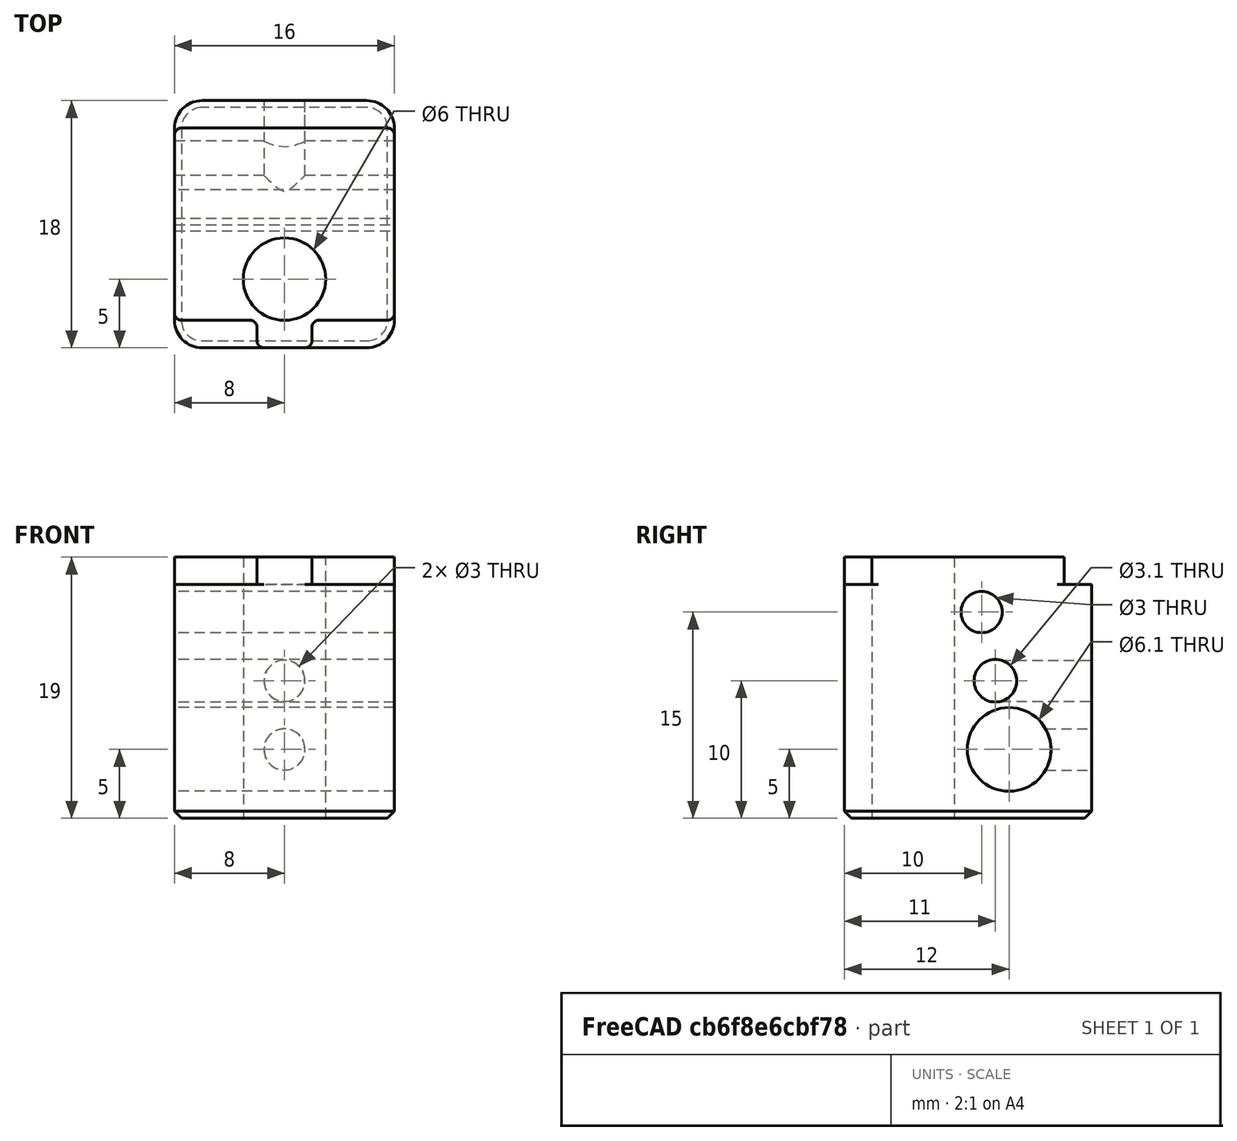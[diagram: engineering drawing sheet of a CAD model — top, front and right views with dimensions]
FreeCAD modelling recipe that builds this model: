
FCSTD DOCUMENT  (FreeCAD 0.17R11850 (Git))
Label: some_struder_heater_block
License: All rights reserved
LicenseURL: http://en.wikipedia.org/wiki/All_rights_reserved
objects: Drawing::FeatureView×33, Sketcher::SketchObject×4, Drawing::FeatureViewPart×4, PartDesign::Pocket×3, PartDesign::Fillet×2, PartDesign::Pad×1, PartDesign::Chamfer×1, PartDesign::Body×1, Drawing::FeaturePage×1
note: 16 computed .brp shape members not serialized (recipe doc carries the construction recipe); baked Part::Feature solids carry a one-line shape summary decoded from their .brp

FEATURE [Sketcher::SketchObject] Sketch
  MapMode = 5
  Support = -> [XY_Plane]
  sketch-geometry (5):
    g0: Circle CenterX=0 CenterY=0 CenterZ=0 NormalX=0 NormalY=0 NormalZ=1 Radius=3
    g1: LineSegment StartX=-8 StartY=13 StartZ=0 EndX=8 EndY=13 EndZ=0
    g2: LineSegment StartX=8 StartY=13 StartZ=0 EndX=8 EndY=-5 EndZ=0
    g3: LineSegment StartX=8 StartY=-5 StartZ=0 EndX=-8 EndY=-5 EndZ=0
    g4: LineSegment StartX=-8 StartY=-5 StartZ=0 EndX=-8 EndY=13 EndZ=0
  constraints (14):
    c: Coincident(g0,g-1)
    c: Coincident(g1,g2)
    c: Coincident(g2,g3)
    c: Coincident(g3,g4)
    c: Coincident(g4,g1)
    c: Horizontal(g1)
    c: Horizontal(g3)
    c: Vertical(g2)
    c: Vertical(g4)
    c: DistanceX(g1,g1) = 16
    c: DistanceY(g2,g2) = 18
    c: Symmetric(g1,g1,g-2)
    c: Radius(g0) = 3
    c: DistanceY(g2) = -5
FEATURE [PartDesign::Pad] Pad
  Length = 19
  Length2 = 100
  Profile = -> Sketch
  Type = 0
FEATURE [Sketcher::SketchObject] Sketch001
  ExternalGeometry = -> [Pad]
  MapMode = 5
  Placement = pos=(-8,0,0) rot=(0.57735,-0.57735,-0.57735;2.0944rad)
  Support = -> [Pad]
  sketch-geometry (3):
    g0: Circle CenterX=-7 CenterY=5 CenterZ=0 NormalX=0 NormalY=0 NormalZ=1 Radius=3.05
    g1: Circle CenterX=-6 CenterY=10 CenterZ=0 NormalX=0 NormalY=0 NormalZ=1 Radius=1.55
    g2: Circle CenterX=-5 CenterY=15 CenterZ=0 NormalX=0 NormalY=0 NormalZ=1 Radius=1.5
  constraints (9):
    c: Radius(g1) = 1.55
    c: Radius(g0) = 3.05
    c: Radius(g2) = 1.5
    c: DistanceY(g0) = 5
    c: DistanceX(g-3,g0) = 6
    c: DistanceY(g0,g1) = 5
    c: DistanceX(g0,g1) = 1
    c: DistanceX(g1,g2) = 1
    c: DistanceY(g1,g2) = 5
FEATURE [PartDesign::Pocket] Pocket
  BaseFeature = -> Pad
  Length = 5
  Profile = -> Sketch001
  Type = 1
FEATURE [Sketcher::SketchObject] Sketch002
  MapMode = 5
  Placement = pos=(0,13,0) rot=(0,0.707107,0.707107;3.14159rad)
  Support = -> [Pocket]
  sketch-geometry (2):
    g0: Circle CenterX=0 CenterY=5 CenterZ=0 NormalX=0 NormalY=0 NormalZ=1 Radius=1.5
    g1: Circle CenterX=0 CenterY=10 CenterZ=0 NormalX=0 NormalY=0 NormalZ=1 Radius=1.5
  constraints (6):
    c: PointOnObject(g0,g-2)
    c: PointOnObject(g1,g-2)
    c: Radius(g0) = 1.5
    c: Equal(g0,g1)
    c: DistanceY(g0) = 5
    c: DistanceY(g0,g1) = 5
FEATURE [PartDesign::Pocket] Pocket001
  BaseFeature = -> Pocket
  Length = 7
  Profile = -> Sketch002
  Type = 0
FEATURE [Sketcher::SketchObject] Sketch003
  ExternalGeometry = -> [Pocket001]
  MapMode = 5
  Placement = pos=(0,0,19) rot=(0,0,1;0rad)
  Support = -> [Pocket001]
  sketch-geometry (12):
    g0: LineSegment StartX=-8 StartY=13 StartZ=0 EndX=8 EndY=13 EndZ=0
    g1: LineSegment StartX=8 StartY=13 StartZ=0 EndX=8 EndY=11 EndZ=0
    g2: LineSegment StartX=8 StartY=11 StartZ=0 EndX=-8 EndY=11 EndZ=0
    g3: LineSegment StartX=-8 StartY=11 StartZ=0 EndX=-8 EndY=13 EndZ=0
    g4: LineSegment StartX=-8 StartY=-3 StartZ=0 EndX=-2 EndY=-3 EndZ=0
    g5: LineSegment StartX=-2 StartY=-3 StartZ=0 EndX=-2 EndY=-5 EndZ=0
    g6: LineSegment StartX=-2 StartY=-5 StartZ=0 EndX=-8 EndY=-5 EndZ=0
    g7: LineSegment StartX=-8 StartY=-5 StartZ=0 EndX=-8 EndY=-3 EndZ=0
    g8: LineSegment StartX=2 StartY=-3 StartZ=0 EndX=8 EndY=-3 EndZ=0
    g9: LineSegment StartX=8 StartY=-3 StartZ=0 EndX=8 EndY=-5 EndZ=0
    g10: LineSegment StartX=8 StartY=-5 StartZ=0 EndX=2 EndY=-5 EndZ=0
    g11: LineSegment StartX=2 StartY=-5 StartZ=0 EndX=2 EndY=-3 EndZ=0
  constraints (33):
    c: Coincident(g0,g1)
    c: Coincident(g1,g2)
    c: Coincident(g2,g3)
    c: Coincident(g3,g0)
    c: Horizontal(g0)
    c: Horizontal(g2)
    c: Vertical(g1)
    c: Vertical(g3)
    c: Coincident(g4,g5)
    c: Coincident(g5,g6)
    c: Coincident(g6,g7)
    c: Coincident(g7,g4)
    c: Horizontal(g4)
    c: Horizontal(g6)
    c: Vertical(g5)
    c: Vertical(g7)
    c: Coincident(g8,g9)
    c: Coincident(g9,g10)
    c: Coincident(g10,g11)
    c: Coincident(g11,g8)
    c: Horizontal(g8)
    c: Horizontal(g10)
    c: Vertical(g9)
    c: Vertical(g11)
    c: Coincident(g9,g-4)
    c: Coincident(g6,g-4)
    c: Coincident(g0,g-3)
    c: Coincident(g0,g-3)
    c: DistanceY(g3,g3) = 2
    c: Equal(g9,g5)
    c: Equal(g5,g1)
    c: DistanceX(g5,g10) = 4
    c: Equal(g8,g4)
FEATURE [PartDesign::Pocket] Pocket002
  BaseFeature = -> Pocket001
  Length = 2
  Profile = -> Sketch003
  Type = 0
FEATURE [PartDesign::Fillet] Fillet
  Base = -> Pocket002 [Edge26,Edge11,Edge4,Edge2]
  BaseFeature = -> Pocket002
  Radius = 2
FEATURE [PartDesign::Fillet] Fillet001
  Base = -> Fillet [Edge26,Edge32,Edge45,Edge44,Edge33,Edge25,Edge54,Edge59]
  BaseFeature = -> Fillet
  Radius = 0.5
FEATURE [PartDesign::Chamfer] Chamfer
  Base = -> Fillet001 [Edge64]
  BaseFeature = -> Fillet001
  Size = 0.5
FEATURE [PartDesign::Body] Body
  Origin = -> BodyOrigin
  Tip = -> Chamfer
FEATURE [Drawing::FeatureViewPart] Ortho  label="Ortho_0_0"
  Direction = (1,0,0)
  HiddenWidth = 0.15
  LineWidth = 0.35
  Rotation = -90
  Scale = 2
  ShowHiddenLines = false
  ShowSmoothLines = false
  Source = -> Chamfer
  Tolerance = 0.05
  ViewResult = <blob: 5438 chars omitted>
  Visible = true
  X = 89.6667
  Y = 128.667
FEATURE [Drawing::FeatureViewPart] Ortho001  label="Ortho_1_1"
  Direction = (0.57735,0.57735,0.57735)
  HiddenWidth = 0.15
  LineWidth = 0.35
  Rotation = 120
  Scale = 2
  ShowHiddenLines = false
  ShowSmoothLines = false
  Source = -> Chamfer
  Tolerance = 0.05
  ViewResult = <blob: 4942 chars omitted>
  Visible = true
  X = 195.676
  Y = 62.5808
FEATURE [Drawing::FeatureViewPart] Ortho002  label="Ortho_1_0"
  Direction = (0,1,0)
  HiddenWidth = 0.15
  LineWidth = 0.35
  Rotation = -90
  Scale = 2
  ShowHiddenLines = false
  ShowSmoothLines = false
  Source = -> Chamfer
  Tolerance = 0.05
  ViewResult = <blob: 5743 chars omitted>
  Visible = true
  X = 201.333
  Y = 128.667
FEATURE [Drawing::FeatureViewPart] Ortho003  label="Ortho_0_1"
  Direction = (0,0,1)
  HiddenWidth = 0.15
  LineWidth = 0.35
  Rotation = 90
  Scale = 2
  ShowHiddenLines = false
  ShowSmoothLines = false
  Source = -> Chamfer
  Tolerance = 0.05
  ViewResult = <g id="Ortho_0_1"\n   transform="rotate(90,89.6667,50.3333) translate(89.6667,50.3333) scale(2,2)"\n  >\n<g   fill="none"\n   stroke="rgb(0, 0, 0)"\n   stroke-linecap="butt"\n   stroke-linejoin="miter"\n   stroke-width="0.125"\n   stroke_width="0.175000"\n   transform="scale(1,-1)"\n  >\n<path id= "1" d=" M 8 11 L 8 10.5 " />\n<path id= "2" d=" M 8 -3 L 8 -2.5 " />\n<path id= "3" d=" M 8 10.5 L 8 -2.5 " />\n<path d="M6 13 A2 2 0 0 0 8 11" /><path id= "5" d=" M -8 11 L -8 10.5 " />\n<path d="M-6 13 A2 2 0 0 1 -8 11" /><path id= "7" d=" M -6 13 L 6 13 " />\n<path d="M8 -3 A2 2 0 0 0 6 -5" /><path d="M8 10.5 A0.5 0.5 0 0 1 7.5 11" /><path id= "10" d=" M 2 -5 L 1.5 -5 " />\n<path id= "11" d=" M 6 -5 L 2 -5 " />\n<path id= "12" d=" M -8 -2.5 L -8 10.5 " />\n<path d="M-8 -2.5 A0.5 0.5 0 0 1 -7.5 -3" /><path d="M-8 10.5 A0.5 0.5 0 0 0 -7.5 11" /><path id= "15" d=" M -7.5 -3 L -2.5 -3 " />\n<path id= "16" d=" M 7.5 11 L -7.5 11 " />\n<path d="M-2.5 -3 A0.5 0.5 0 0 0 -2 -3.5" /><path id= "18" d=" M -2 -3.5 L -2 -4.5 " />\n<path d="M-1.5 -5 A0.5 0.5 0 0 0 -2 -4.5" /><path d="M8 -2.5 A0.5 0.5 0 0 0 7.5 -3" /><path id= "21" d=" M 1.5 -5 L -1.5 -5 " />\n<path id= "22" d=" M 2.5 -3 L 7.5 -3 " />\n<path d="M1.5 -5 A0.5 0.5 0 0 1 2 -4.5" /><path d="M2.5 -3 A0.5 0.5 0 0 1 2 -3.5" /><path id= "25" d=" M 2 -4.5 L 2 -3.5 " />\n<circle cx ="0" cy ="0" r ="3" /><path id= "27" d=" M -8 -3 L -8 -2.5 " />\n<path id= "28" d=" M -2 -5 L -6 -5 " />\n<path id= "29" d=" M -2 -5 L -1.5 -5 " />\n<path d="M-8 -3 A2 2 0 0 1 -6 -5" /></g>\n</g>
  Visible = true
  X = 89.6667
  Y = 50.3333
FEATURE [Drawing::FeatureView] dim001
  Rotation = 0
  ViewResult = <g> <line x1="115.666700" y1="36.333300" x2="115.666700" y2="19.397439" style="stroke:rgb(0,0,255);stroke-width:0.20" />\n<line x1="79.666700" y1="36.333300" x2="79.666700" y2="19.397439" style="stroke:rgb(0,0,255);stroke-width:0.20" />\n<line x1="115.666700" y1="20.397439" x2="79.666700" y2="20.397439" style="stroke:rgb(0,0,255);stroke-width:0.20" />\n<polygon points="115.666700,20.397439 112.666700,19.647439 112.666700,20.397439 112.666700,21.147439" style="fill:rgb(0,0,255);stroke:rgb(0,0,255);stroke-width:0" />\n<polygon points="79.666700,20.397439 82.666700,21.147439 82.666700,20.397439 82.666700,19.647439" style="fill:rgb(0,0,255);stroke:rgb(0,0,255);stroke-width:0" />\n<text x="97.666700" y="19.397439" font-family="Verdana" font-size="3" fill="rgb(0,0,255)" text-anchor="middle"  >18.00</text> </g> 
  Visible = true
  X = 0
  Y = 0
FEATURE [Drawing::FeatureView] dim002
  Rotation = 0
  ViewResult = <g> <line x1="82.666700" y1="34.333300" x2="59.209307" y2="34.333300" style="stroke:rgb(0,0,255);stroke-width:0.20" />\n<line x1="82.666700" y1="66.333300" x2="59.209307" y2="66.333300" style="stroke:rgb(0,0,255);stroke-width:0.20" />\n<line x1="60.209307" y1="34.333300" x2="60.209307" y2="66.333300" style="stroke:rgb(0,0,255);stroke-width:0.20" />\n<polygon points="60.209307,34.333300 59.459307,37.333300 60.209307,37.333300 60.959307,37.333300" style="fill:rgb(0,0,255);stroke:rgb(0,0,255);stroke-width:0" />\n<polygon points="60.209307,66.333300 60.959307,63.333300 60.209307,63.333300 59.459307,63.333300" style="fill:rgb(0,0,255);stroke:rgb(0,0,255);stroke-width:0" />\n<text x="59.209307" y="50.333300" font-family="Verdana" font-size="3" fill="rgb(0,0,255)" text-anchor="middle" transform="rotate(-90.000000 59.209307,50.333300)" >16.00</text> </g> 
  Visible = true
  X = 0
  Y = 0
FEATURE [Drawing::FeatureView] dim003
  Rotation = 0
  ViewResult = <g> <line x1="82.666700" y1="90.667000" x2="59.946563" y2="90.667000" style="stroke:rgb(0,0,255);stroke-width:0.20" />\n<line x1="81.666700" y1="128.667000" x2="59.946563" y2="128.667000" style="stroke:rgb(0,0,255);stroke-width:0.20" />\n<line x1="60.946563" y1="90.667000" x2="60.946563" y2="128.667000" style="stroke:rgb(0,0,255);stroke-width:0.20" />\n<polygon points="60.946563,90.667000 60.196563,93.667000 60.946563,93.667000 61.696563,93.667000" style="fill:rgb(0,0,255);stroke:rgb(0,0,255);stroke-width:0" />\n<polygon points="60.946563,128.667000 61.696563,125.667000 60.946563,125.667000 60.196563,125.667000" style="fill:rgb(0,0,255);stroke:rgb(0,0,255);stroke-width:0" />\n<text x="59.946563" y="109.667000" font-family="Verdana" font-size="3" fill="rgb(0,0,255)" text-anchor="middle" transform="rotate(-90.000000 59.946563,109.667000)" >19.00</text> </g> 
  Visible = true
  X = 0
  Y = 0
FEATURE [Drawing::FeatureView] dim004
  Rotation = 0
  ViewResult = <g> <line x1="111.666700" y1="67.333300" x2="111.666700" y2="76.937452" style="stroke:rgb(0,0,255);stroke-width:0.20" />\n<line x1="115.666700" y1="64.333300" x2="115.666700" y2="76.937452" style="stroke:rgb(0,0,255);stroke-width:0.20" />\n<line x1="111.666700" y1="75.937452" x2="115.666700" y2="75.937452" style="stroke:rgb(0,0,255);stroke-width:0.20" />\n<polygon points="111.666700,75.937452 108.666700,75.187452 108.666700,75.937452 108.666700,76.687452" style="fill:rgb(0,0,255);stroke:rgb(0,0,255);stroke-width:0" />\n<polygon points="115.666700,75.937452 118.666700,76.687452 118.666700,75.937452 118.666700,75.187452" style="fill:rgb(0,0,255);stroke:rgb(0,0,255);stroke-width:0" />\n<text x="113.666700" y="74.937452" font-family="Verdana" font-size="3" fill="rgb(0,0,255)" text-anchor="middle"  >2.0</text> </g> 
  Visible = true
  X = 0
  Y = 0
FEATURE [Drawing::FeatureView] dim005
  Rotation = 0
  ViewResult = <g> <line x1="83.666700" y1="67.333300" x2="83.666700" y2="75.954443" style="stroke:rgb(0,0,255);stroke-width:0.20" />\n<line x1="79.666700" y1="64.333300" x2="79.666700" y2="75.954443" style="stroke:rgb(0,0,255);stroke-width:0.20" />\n<line x1="83.666700" y1="74.954443" x2="79.666700" y2="74.954443" style="stroke:rgb(0,0,255);stroke-width:0.20" />\n<polygon points="83.666700,74.954443 86.666700,75.704443 86.666700,74.954443 86.666700,74.204443" style="fill:rgb(0,0,255);stroke:rgb(0,0,255);stroke-width:0" />\n<polygon points="79.666700,74.954443 76.666700,74.204443 76.666700,74.954443 76.666700,75.704443" style="fill:rgb(0,0,255);stroke:rgb(0,0,255);stroke-width:0" />\n<text x="81.666700" y="73.954443" font-family="Verdana" font-size="3" fill="rgb(0,0,255)" text-anchor="middle"  >2.0</text> </g> 
  Visible = true
  X = 0
  Y = 0
FEATURE [Drawing::FeatureView] dim006
  Rotation = 0
  ViewResult = <g> <line x1="78.666700" y1="54.333300" x2="73.318650" y2="54.333300" style="stroke:rgb(0,0,255);stroke-width:0.20" />\n<line x1="82.666700" y1="66.333300" x2="73.318650" y2="66.333300" style="stroke:rgb(0,0,255);stroke-width:0.20" />\n<line x1="74.318650" y1="54.333300" x2="74.318650" y2="66.333300" style="stroke:rgb(0,0,255);stroke-width:0.20" />\n<polygon points="74.318650,54.333300 73.568650,57.333300 74.318650,57.333300 75.068650,57.333300" style="fill:rgb(0,0,255);stroke:rgb(0,0,255);stroke-width:0" />\n<polygon points="74.318650,66.333300 75.068650,63.333300 74.318650,63.333300 73.568650,63.333300" style="fill:rgb(0,0,255);stroke:rgb(0,0,255);stroke-width:0" />\n<text x="73.318650" y="60.333300" font-family="Verdana" font-size="3" fill="rgb(0,0,255)" text-anchor="middle" transform="rotate(-90.000000 73.318650,60.333300)" >6.0</text> </g> 
  Visible = true
  X = 0
  Y = 0
FEATURE [Drawing::FeatureView] dim007
  Rotation = 0
  ViewResult = <g> <line x1="82.666700" y1="34.333300" x2="73.236349" y2="34.333300" style="stroke:rgb(0,0,255);stroke-width:0.20" />\n<line x1="78.666700" y1="46.333300" x2="73.236349" y2="46.333300" style="stroke:rgb(0,0,255);stroke-width:0.20" />\n<line x1="74.236349" y1="34.333300" x2="74.236349" y2="46.333300" style="stroke:rgb(0,0,255);stroke-width:0.20" />\n<polygon points="74.236349,34.333300 73.486349,37.333300 74.236349,37.333300 74.986349,37.333300" style="fill:rgb(0,0,255);stroke:rgb(0,0,255);stroke-width:0" />\n<polygon points="74.236349,46.333300 74.986349,43.333300 74.236349,43.333300 73.486349,43.333300" style="fill:rgb(0,0,255);stroke:rgb(0,0,255);stroke-width:0" />\n<text x="73.236349" y="40.333300" font-family="Verdana" font-size="3" fill="rgb(0,0,255)" text-anchor="middle" transform="rotate(-90.000000 73.236349,40.333300)" >6.0</text> </g> 
  Visible = true
  X = 0
  Y = 0
FEATURE [Drawing::FeatureView] dim008
  Rotation = 0
  ViewResult = <g> \n  <line x1="89.666700" y1="52.333300" x2="89.666700" y2="83.071088" style="stroke:rgb(0,0,255);stroke-width:0.20" />\n<line x1="79.666700" y1="64.333300" x2="79.666700" y2="83.071088" style="stroke:rgb(0,0,255);stroke-width:0.20" />\n<line x1="89.666700" y1="82.071088" x2="79.666700" y2="82.071088" style="stroke:rgb(0,0,255);stroke-width:0.20" /> \n  <polygon points="79.666700,82.071088 82.666700,82.821088 82.666700,82.071088 82.666700,81.321088" style="fill:rgb(0,0,255);stroke:rgb(0,0,255);stroke-width:0" /><polygon points="89.666700,82.071088 86.666700,81.321088 86.666700,82.071088 86.666700,82.821088" style="fill:rgb(0,0,255);stroke:rgb(0,0,255);stroke-width:0" /> \n  <text x="84.666700" y="81.071088" font-family="Verdana" font-size="3" fill="rgb(0,0,255)" text-anchor="middle"  >5.00</text> </g>
  Visible = true
  X = 0
  Y = 0
FEATURE [Drawing::FeatureView] dim009
  Rotation = 0
  ViewResult = <g> \n  <line x1="91.666700" y1="50.333300" x2="130.872459" y2="50.333300" style="stroke:rgb(0,0,255);stroke-width:0.20" />\n<line x1="86.666700" y1="66.333300" x2="130.872459" y2="66.333300" style="stroke:rgb(0,0,255);stroke-width:0.20" />\n<line x1="129.872459" y1="50.333300" x2="129.872459" y2="66.333300" style="stroke:rgb(0,0,255);stroke-width:0.20" /> \n  <polygon points="129.872459,66.333300 130.622459,63.333300 129.872459,63.333300 129.122459,63.333300" style="fill:rgb(0,0,255);stroke:rgb(0,0,255);stroke-width:0" /><polygon points="129.872459,50.333300 129.122459,53.333300 129.872459,53.333300 130.622459,53.333300" style="fill:rgb(0,0,255);stroke:rgb(0,0,255);stroke-width:0" /> \n  <text x="128.872459" y="58.333300" font-family="Verdana" font-size="3" fill="rgb(0,0,255)" text-anchor="middle" transform="rotate(-90.000000 128.872459,58.333300)" >8.00</text> </g>
  Visible = true
  X = 0
  Y = 0
FEATURE [Drawing::FeatureView] dim013
  Rotation = 0
  ViewResult = <g> <line x1="112.666700" y1="90.667000" x2="122.712296" y2="90.667000" style="stroke:rgb(0,0,255);stroke-width:0.20" />\n<line x1="114.556726" y1="94.667000" x2="122.712296" y2="94.667000" style="stroke:rgb(0,0,255);stroke-width:0.20" />\n<line x1="121.712296" y1="90.667000" x2="121.712296" y2="94.667000" style="stroke:rgb(0,0,255);stroke-width:0.20" />\n<polygon points="121.712296,90.667000 122.462296,87.667000 121.712296,87.667000 120.962296,87.667000" style="fill:rgb(0,0,255);stroke:rgb(0,0,255);stroke-width:0" />\n<polygon points="121.712296,94.667000 120.962296,97.667000 121.712296,97.667000 122.462296,97.667000" style="fill:rgb(0,0,255);stroke:rgb(0,0,255);stroke-width:0" />\n<text x="120.712296" y="92.667000" font-family="Verdana" font-size="3" fill="rgb(0,0,255)" text-anchor="middle" transform="rotate(-90.000000 120.712296,92.667000)" >2.0</text> </g> 
  Visible = true
  X = 0
  Y = 0
FEATURE [Drawing::FeatureView] dim014
  Rotation = 0
  ViewResult = <g> \n  <line x1="78.666700" y1="90.667000" x2="72.989443" y2="90.667000" style="stroke:rgb(0,0,255);stroke-width:0.20" />\n<line x1="79.931160" y1="94.667000" x2="72.989443" y2="94.667000" style="stroke:rgb(0,0,255);stroke-width:0.20" />\n<line x1="73.989443" y1="90.667000" x2="73.989443" y2="94.667000" style="stroke:rgb(0,0,255);stroke-width:0.20" /> \n  <polygon points="73.989443,94.667000 73.239443,97.667000 73.989443,97.667000 74.739443,97.667000" style="fill:rgb(0,0,255);stroke:rgb(0,0,255);stroke-width:0" /><polygon points="73.989443,90.667000 74.739443,87.667000 73.989443,87.667000 73.239443,87.667000" style="fill:rgb(0,0,255);stroke:rgb(0,0,255);stroke-width:0" /> \n  <text x="72.989443" y="92.667000" font-family="Verdana" font-size="3" fill="rgb(0,0,255)" text-anchor="middle" transform="rotate(-90.000000 72.989443,92.667000)" >2.0</text> </g>
  Visible = true
  X = 0
  Y = 0
FEATURE [Drawing::FeatureView] dim015
  Rotation = 0
  ViewResult = <g> <line x1="79.666700" y1="129.667000" x2="79.666700" y2="134.703211" style="stroke:rgb(0,0,255);stroke-width:0.20" />\n<line x1="99.666700" y1="100.667033" x2="99.666700" y2="134.703211" style="stroke:rgb(0,0,255);stroke-width:0.20" />\n<line x1="79.666700" y1="133.703211" x2="99.666700" y2="133.703211" style="stroke:rgb(0,0,255);stroke-width:0.20" />\n<polygon points="79.666700,133.703211 82.666700,134.453211 82.666700,133.703211 82.666700,132.953211" style="fill:rgb(0,0,255);stroke:rgb(0,0,255);stroke-width:0" />\n<polygon points="99.666700,133.703211 96.666700,132.953211 96.666700,133.703211 96.666700,134.453211" style="fill:rgb(0,0,255);stroke:rgb(0,0,255);stroke-width:0" />\n<text x="89.666700" y="132.703211" font-family="Verdana" font-size="3" fill="rgb(0,0,255)" text-anchor="middle"  >10.00</text> </g> 
  Visible = true
  X = 0
  Y = 0
FEATURE [Drawing::FeatureView] dim016
  Rotation = 0
  ViewResult = <g> <line x1="79.666700" y1="129.667000" x2="79.666700" y2="140.600943" style="stroke:rgb(0,0,255);stroke-width:0.20" />\n<line x1="101.666700" y1="110.667033" x2="101.666700" y2="140.600943" style="stroke:rgb(0,0,255);stroke-width:0.20" />\n<line x1="79.666700" y1="139.600943" x2="101.666700" y2="139.600943" style="stroke:rgb(0,0,255);stroke-width:0.20" />\n<polygon points="79.666700,139.600943 82.666700,140.350943 82.666700,139.600943 82.666700,138.850943" style="fill:rgb(0,0,255);stroke:rgb(0,0,255);stroke-width:0" />\n<polygon points="101.666700,139.600943 98.666700,138.850943 98.666700,139.600943 98.666700,140.350943" style="fill:rgb(0,0,255);stroke:rgb(0,0,255);stroke-width:0" />\n<text x="90.666700" y="138.600943" font-family="Verdana" font-size="3" fill="rgb(0,0,255)" text-anchor="middle"  >11.00</text> </g> 
  Visible = true
  X = 0
  Y = 0
FEATURE [Drawing::FeatureView] dim017
  Rotation = 0
  ViewResult = <g> <line x1="79.666700" y1="129.667000" x2="79.666700" y2="147.598056" style="stroke:rgb(0,0,255);stroke-width:0.20" />\n<line x1="103.666700" y1="120.667033" x2="103.666700" y2="147.598056" style="stroke:rgb(0,0,255);stroke-width:0.20" />\n<line x1="79.666700" y1="146.598056" x2="103.666700" y2="146.598056" style="stroke:rgb(0,0,255);stroke-width:0.20" />\n<polygon points="79.666700,146.598056 82.666700,147.348056 82.666700,146.598056 82.666700,145.848056" style="fill:rgb(0,0,255);stroke:rgb(0,0,255);stroke-width:0" />\n<polygon points="103.666700,146.598056 100.666700,145.848056 100.666700,146.598056 100.666700,147.348056" style="fill:rgb(0,0,255);stroke:rgb(0,0,255);stroke-width:0" />\n<text x="91.666700" y="145.598056" font-family="Verdana" font-size="3" fill="rgb(0,0,255)" text-anchor="middle"  >12.00</text> </g> 
  Visible = true
  X = 0
  Y = 0
FEATURE [Drawing::FeatureView] dim019
  Rotation = 0
  ViewResult = <g> <line x1="185.333000" y1="129.667000" x2="185.333000" y2="141.538790" style="stroke:rgb(0,0,255);stroke-width:0.20" />\n<line x1="201.333000" y1="120.667033" x2="201.333000" y2="141.538790" style="stroke:rgb(0,0,255);stroke-width:0.20" />\n<line x1="185.333000" y1="140.538790" x2="201.333000" y2="140.538790" style="stroke:rgb(0,0,255);stroke-width:0.20" />\n<polygon points="185.333000,140.538790 188.333000,141.288790 188.333000,140.538790 188.333000,139.788790" style="fill:rgb(0,0,255);stroke:rgb(0,0,255);stroke-width:0" />\n<polygon points="201.333000,140.538790 198.333000,139.788790 198.333000,140.538790 198.333000,141.288790" style="fill:rgb(0,0,255);stroke:rgb(0,0,255);stroke-width:0" />\n<text x="193.333000" y="139.538790" font-family="Verdana" font-size="3" fill="rgb(0,0,255)" text-anchor="middle"  >8.00</text> </g> 
  Visible = true
  X = 0
  Y = 0
FEATURE [Drawing::FeatureView] dim020
  Rotation = 0
  ViewResult = <g> <line x1="187.333000" y1="128.667000" x2="174.796941" y2="128.667000" style="stroke:rgb(0,0,255);stroke-width:0.20" />\n<line x1="199.332976" y1="118.667000" x2="174.796941" y2="118.667000" style="stroke:rgb(0,0,255);stroke-width:0.20" />\n<line x1="175.796941" y1="128.667000" x2="175.796941" y2="118.667000" style="stroke:rgb(0,0,255);stroke-width:0.20" />\n<polygon points="175.796941,128.667000 176.546941,125.667000 175.796941,125.667000 175.046941,125.667000" style="fill:rgb(0,0,255);stroke:rgb(0,0,255);stroke-width:0" />\n<polygon points="175.796941,118.667000 175.046941,121.667000 175.796941,121.667000 176.546941,121.667000" style="fill:rgb(0,0,255);stroke:rgb(0,0,255);stroke-width:0" />\n<text x="174.796941" y="123.667000" font-family="Verdana" font-size="3" fill="rgb(0,0,255)" text-anchor="middle" transform="rotate(-90.000000 174.796941,123.667000)" >5.00</text> </g> 
  Visible = true
  X = 0
  Y = 0
FEATURE [Drawing::FeatureView] dim021
  Rotation = 0
  ViewResult = <g> \n  <line x1="199.333000" y1="118.667000" x2="174.698178" y2="118.667000" style="stroke:rgb(0,0,255);stroke-width:0.20" />\n<line x1="199.333000" y1="108.667000" x2="174.698178" y2="108.667000" style="stroke:rgb(0,0,255);stroke-width:0.20" />\n<line x1="175.698178" y1="118.667000" x2="175.698178" y2="108.667000" style="stroke:rgb(0,0,255);stroke-width:0.20" /> \n  <polygon points="175.698178,108.667000 174.948178,111.667000 175.698178,111.667000 176.448178,111.667000" style="fill:rgb(0,0,255);stroke:rgb(0,0,255);stroke-width:0" /><polygon points="175.698178,118.667000 176.448178,115.667000 175.698178,115.667000 174.948178,115.667000" style="fill:rgb(0,0,255);stroke:rgb(0,0,255);stroke-width:0" /> \n  <text x="174.698178" y="113.667000" font-family="Verdana" font-size="3" fill="rgb(0,0,255)" text-anchor="middle" transform="rotate(-90.000000 174.698178,113.667000)" >5.00</text> </g>
  Visible = true
  X = 0
  Y = 0
FEATURE [Drawing::FeatureView] dim022
  Rotation = 0
  ViewResult = <g> <line x1="184.333000" y1="90.667000" x2="173.927832" y2="90.667000" style="stroke:rgb(0,0,255);stroke-width:0.20" />\n<line x1="187.333000" y1="94.667000" x2="173.927832" y2="94.667000" style="stroke:rgb(0,0,255);stroke-width:0.20" />\n<line x1="174.927832" y1="90.667000" x2="174.927832" y2="94.667000" style="stroke:rgb(0,0,255);stroke-width:0.20" />\n<polygon points="174.927832,90.667000 175.677832,87.667000 174.927832,87.667000 174.177832,87.667000" style="fill:rgb(0,0,255);stroke:rgb(0,0,255);stroke-width:0" />\n<polygon points="174.927832,94.667000 174.177832,97.667000 174.927832,97.667000 175.677832,97.667000" style="fill:rgb(0,0,255);stroke:rgb(0,0,255);stroke-width:0" />\n<text x="173.927832" y="92.667000" font-family="Verdana" font-size="3" fill="rgb(0,0,255)" text-anchor="middle" transform="rotate(-90.000000 173.927832,92.667000)" >2.0</text> </g> 
  Visible = true
  X = 0
  Y = 0
FEATURE [Drawing::FeatureView] dim010
  Rotation = 0
  ViewResult = <g>  <circle cx ="101.666700" cy ="108.667000" r="0.000000" stroke="none" fill="rgb(0,0,255)" /> \n<line x1="119.648056" y1="102.261698" x2="98.746447" y2="109.707250" style="stroke:rgb(0,0,255);stroke-width:0.20" />\n<polygon points="104.586953,107.626750 101.509228,107.926931 101.760902,108.633444 102.012575,109.339956" style="fill:rgb(0,0,255);stroke:rgb(0,0,255);stroke-width:0" />\n<polygon points="98.746447,109.707250 101.824172,109.407069 101.572498,108.700556 101.320825,107.994044" style="fill:rgb(0,0,255);stroke:rgb(0,0,255);stroke-width:0" />\n<line x1="119.648056" y1="102.261698" x2="144.138517" y2="102.261698" style="stroke:rgb(0,0,255);stroke-width:0.20" />\n<text x="131.893286" y="101.261698" font-family="Verdana" font-size="3" fill="rgb(0,0,255)" text-anchor="middle" transform="rotate(0.000000 131.893286,101.261698)" >Ø3.1</text> </g>
  Visible = true
  X = 0
  Y = 0
FEATURE [Drawing::FeatureView] dim011
  Rotation = 0
  ViewResult = <g>  <circle cx ="103.666700" cy ="118.667000" r="0.000000" stroke="none" fill="rgb(0,0,255)" /> \n<line x1="120.395856" y1="112.170052" x2="97.980458" y2="120.875313" style="stroke:rgb(0,0,255);stroke-width:0.20" />\n<polygon points="109.352942,116.458687 106.284916,116.845614 106.556430,117.544742 106.827944,118.243871" style="fill:rgb(0,0,255);stroke:rgb(0,0,255);stroke-width:0" />\n<polygon points="97.980458,120.875313 101.048484,120.488386 100.776970,119.789258 100.505456,119.090129" style="fill:rgb(0,0,255);stroke:rgb(0,0,255);stroke-width:0" />\n<line x1="120.395856" y1="112.170052" x2="143.764617" y2="112.170052" style="stroke:rgb(0,0,255);stroke-width:0.20" />\n<text x="132.080236" y="111.170052" font-family="Verdana" font-size="3" fill="rgb(0,0,255)" text-anchor="middle" transform="rotate(0.000000 132.080236,111.170052)" >Ø6.1</text> </g>
  Visible = true
  X = 0
  Y = 0
FEATURE [Drawing::FeatureView] dim012
  Rotation = 0
  ViewResult = <g> <line x1="81.666700" y1="128.667000" x2="75.649536" y2="128.667000" style="stroke:rgb(0,0,255);stroke-width:0.20" />\n<line x1="101.666672" y1="118.667000" x2="75.649536" y2="118.667000" style="stroke:rgb(0,0,255);stroke-width:0.20" />\n<line x1="76.649536" y1="128.667000" x2="76.649536" y2="118.667000" style="stroke:rgb(0,0,255);stroke-width:0.20" />\n<polygon points="76.649536,128.667000 77.399536,125.667000 76.649536,125.667000 75.899536,125.667000" style="fill:rgb(0,0,255);stroke:rgb(0,0,255);stroke-width:0" />\n<polygon points="76.649536,118.667000 75.899536,121.667000 76.649536,121.667000 77.399536,121.667000" style="fill:rgb(0,0,255);stroke:rgb(0,0,255);stroke-width:0" />\n<text x="75.649536" y="123.667000" font-family="Verdana" font-size="3" fill="rgb(0,0,255)" text-anchor="middle" transform="rotate(-90.000000 75.649536,123.667000)" >5.00</text> </g> 
  Visible = true
  X = 0
  Y = 0
FEATURE [Drawing::FeatureView] dim018
  Rotation = 0
  ViewResult = <g> <line x1="81.666700" y1="128.667000" x2="69.106283" y2="128.667000" style="stroke:rgb(0,0,255);stroke-width:0.20" />\n<line x1="99.666672" y1="108.667000" x2="69.106283" y2="108.667000" style="stroke:rgb(0,0,255);stroke-width:0.20" />\n<line x1="70.106283" y1="128.667000" x2="70.106283" y2="108.667000" style="stroke:rgb(0,0,255);stroke-width:0.20" />\n<polygon points="70.106283,128.667000 70.856283,125.667000 70.106283,125.667000 69.356283,125.667000" style="fill:rgb(0,0,255);stroke:rgb(0,0,255);stroke-width:0" />\n<polygon points="70.106283,108.667000 69.356283,111.667000 70.106283,111.667000 70.856283,111.667000" style="fill:rgb(0,0,255);stroke:rgb(0,0,255);stroke-width:0" />\n<text x="69.106283" y="118.667000" font-family="Verdana" font-size="3" fill="rgb(0,0,255)" text-anchor="middle" transform="rotate(-90.000000 69.106283,118.667000)" >10.00</text> </g> 
  Visible = true
  X = 0
  Y = 0
FEATURE [Drawing::FeatureView] dim023
  Rotation = 0
  ViewResult = <g> <line x1="81.666700" y1="128.667000" x2="64.619481" y2="128.667000" style="stroke:rgb(0,0,255);stroke-width:0.20" />\n<line x1="97.666672" y1="98.667000" x2="64.619481" y2="98.667000" style="stroke:rgb(0,0,255);stroke-width:0.20" />\n<line x1="65.619481" y1="128.667000" x2="65.619481" y2="98.667000" style="stroke:rgb(0,0,255);stroke-width:0.20" />\n<polygon points="65.619481,128.667000 66.369481,125.667000 65.619481,125.667000 64.869481,125.667000" style="fill:rgb(0,0,255);stroke:rgb(0,0,255);stroke-width:0" />\n<polygon points="65.619481,98.667000 64.869481,101.667000 65.619481,101.667000 66.369481,101.667000" style="fill:rgb(0,0,255);stroke:rgb(0,0,255);stroke-width:0" />\n<text x="64.619481" y="113.667000" font-family="Verdana" font-size="3" fill="rgb(0,0,255)" text-anchor="middle" transform="rotate(-90.000000 64.619481,113.667000)" >15.00</text> </g> 
  Visible = true
  X = 0
  Y = 0
FEATURE [Drawing::FeatureView] dim024
  Rotation = 0
  ViewResult = <g>  <circle cx ="89.666700" cy ="50.333300" r="0.000000" stroke="none" fill="rgb(0,0,255)" /> \n<line x1="123.760958" y1="39.072568" x2="83.969407" y2="52.215015" style="stroke:rgb(0,0,255);stroke-width:0.20" />\n<polygon points="95.363993,48.451585 92.280132,48.680281 92.515346,49.392442 92.750561,50.104604" style="fill:rgb(0,0,255);stroke:rgb(0,0,255);stroke-width:0" />\n<polygon points="83.969407,52.215015 87.053268,51.986319 86.818054,51.274158 86.582839,50.561996" style="fill:rgb(0,0,255);stroke:rgb(0,0,255);stroke-width:0" />\n<line x1="123.760958" y1="39.072568" x2="142.455966" y2="39.072568" style="stroke:rgb(0,0,255);stroke-width:0.20" />\n<text x="133.108462" y="38.072568" font-family="Verdana" font-size="3" fill="rgb(0,0,255)" text-anchor="middle"  >M6X1 THRU</text> </g>
  Visible = true
  X = 0
  Y = 0
FEATURE [Drawing::FeatureView] dim025
  Rotation = 0
  ViewResult = <g>  <circle cx ="99.666700" cy ="98.667000" r="0.000000" stroke="none" fill="rgb(0,0,255)" /> \n<line x1="116.656854" y1="83.005839" x2="97.460863" y2="100.700294" style="stroke:rgb(0,0,255);stroke-width:0.20" />\n<polygon points="101.872537,96.633706 104.586698,95.151872 104.078374,94.600413 103.570051,94.048954" style="fill:rgb(0,0,255);stroke:rgb(0,0,255);stroke-width:0" />\n<polygon points="97.460863,100.700294 94.746702,102.182128 95.255026,102.733587 95.763349,103.285046" style="fill:rgb(0,0,255);stroke:rgb(0,0,255);stroke-width:0" />\n<line x1="116.656854" y1="83.005839" x2="143.203767" y2="83.005839" style="stroke:rgb(0,0,255);stroke-width:0.20" />\n<text x="129.930310" y="82.005839" font-family="Verdana" font-size="3" fill="rgb(0,0,255)" text-anchor="middle"  >M3X0.5 THRU</text> </g>
  Visible = true
  X = 0
  Y = 0
FEATURE [Drawing::FeatureView] dim026
  Rotation = 0
  ViewResult = <g>  <circle cx ="201.333000" cy ="108.667000" r="0.000000" stroke="none" fill="rgb(0,0,255)" /> \n<line x1="222.283653" y1="96.092345" x2="198.760752" y2="110.210872" style="stroke:rgb(0,0,255);stroke-width:0.20" />\n<polygon points="203.905248,107.123128 206.863464,106.222318 206.477496,105.579256 206.091528,104.936194" style="fill:rgb(0,0,255);stroke:rgb(0,0,255);stroke-width:0" />\n<polygon points="198.760752,110.210872 195.802536,111.111682 196.188504,111.754744 196.574472,112.397806" style="fill:rgb(0,0,255);stroke:rgb(0,0,255);stroke-width:0" />\n<line x1="222.283653" y1="96.092345" x2="240.417812" y2="96.092345" style="stroke:rgb(0,0,255);stroke-width:0.20" />\n<text x="231.350733" y="95.092345" font-family="Verdana" font-size="3" fill="rgb(0,0,255)" text-anchor="middle"  >M3X0.5 THRU</text> </g>
  Visible = true
  X = 0
  Y = 0
FEATURE [Drawing::FeatureView] dim027
  Rotation = 0
  ViewResult = <g>  <circle cx ="201.333000" cy ="118.667000" r="0.000000" stroke="none" fill="rgb(0,0,255)" /> \n<line x1="223.218404" y1="105.813749" x2="198.746138" y2="120.186258" style="stroke:rgb(0,0,255);stroke-width:0.20" />\n<polygon points="203.919862,117.147742 206.886538,116.275199 206.506724,115.628483 206.126909,114.981768" style="fill:rgb(0,0,255);stroke:rgb(0,0,255);stroke-width:0" />\n<polygon points="198.746138,120.186258 195.779462,121.058801 196.159276,121.705517 196.539091,122.352232" style="fill:rgb(0,0,255);stroke:rgb(0,0,255);stroke-width:0" />\n<line x1="223.218404" y1="105.813749" x2="239.483061" y2="105.813749" style="stroke:rgb(0,0,255);stroke-width:0.20" />\n<text x="231.350733" y="104.813749" font-family="Verdana" font-size="3" fill="rgb(0,0,255)" text-anchor="middle"  >M3x0.5 THRU</text> </g>
  Visible = true
  X = 0
  Y = 0
FEATURE [Drawing::FeatureView] dimLine001
  Rotation = 0
  ViewResult = <g   >\n<line x1="122.466549" y1="139.464414" x2="115.166700" y2="128.167000" style="stroke:rgb(0,0,255);stroke-width:0.20" />\n<polygon points="115.166700,128.167000 116.164905,131.093788 116.794843,130.686752 117.424781,130.279716" style="fill:rgb(0,0,255);stroke:rgb(0,0,255);stroke-width:0" />\n<line x1="122.466549" y1="139.464414" x2="158.919802" y2="139.464414" style="stroke:rgb(0,0,255);stroke-width:0.20" />\n</g> 
  Visible = true
  X = 0
  Y = 0
FEATURE [Drawing::FeatureView] dimText001
  Rotation = 0
  ViewResult = <g> <text x="128.610355" y="138.235653" font-family="inherit" font-size="3" fill="rgb(0,0,255)" text-anchor="inherit" transform="rotate(0.000000 128.610355,138.235653)" >Chamfer 0.5mm</text> </g>
  Visible = true
  X = 0
  Y = 0
FEATURE [Drawing::FeatureView] dimText002
  Rotation = 0
  ViewResult = <g> <text x="15.000000" y="170.000000" font-family="inherit" font-size="4" fill="rgb(0,0,0)" text-anchor="inherit" transform="rotate(0.000000 15.000000,170.000000)" >NOTES:</text> </g>
  Visible = true
  X = 0
  Y = 0
FEATURE [Drawing::FeatureView] dimText003
  Rotation = 0
  ViewResult = <g> <text x="20.000000" y="180.000000" font-family="inherit" font-size="3" fill="rgb(0,0,0)" text-anchor="inherit" transform="rotate(0.000000 20.000000,180.000000)" >Break all sharp edges</text> </g>
  Visible = true
  X = 0
  Y = 0
FEATURE [Drawing::FeatureView] dimText004
  Rotation = 0
  ViewResult = <g> <text x="20.000000" y="185.000000" font-family="inherit" font-size="3" fill="rgb(0,0,0)" text-anchor="inherit" transform="rotate(0.000000 20.000000,185.000000)" >Lightly spot face all threaded holes</text> </g>
  Visible = true
  X = 0
  Y = 0
FEATURE [Drawing::FeatureView] dimText005
  Rotation = 0
  ViewResult = <g> <text x="20.000000" y="190.000000" font-family="inherit" font-size="3" fill="rgb(0,0,0)" text-anchor="inherit" transform="rotate(0.000000 20.000000,190.000000)" >Parts must be clean and free of oil and debris</text> </g>
  Visible = true
  X = 0
  Y = 0
FEATURE [Drawing::FeaturePage] Page
  EditableTexts = BALDWIN | 7/18/17 | N/A | AO some-struder block | IR | PP-MP0175 | 1 of 1 | 6061 Aluminum
  Group = -> [Ortho,Ortho001,Ortho002,Ortho003,dim001,dim002,dim003,dim004,dim005,dim006,dim007,dim008,dim009,dim013,dim014,dim015,dim016,dim017,dim019,dim020,dim021,dim022,dim010,dim011,dim012,dim018,dim023,dim024,dim025,dim026,dim027,dimLine001,dimText001,dimText002,dimText003,dimText004,dimText005]
  Template = <userpath>/shared-j/Documents/R&D/titleblocks/A4_Landscape_Aleph.svg
